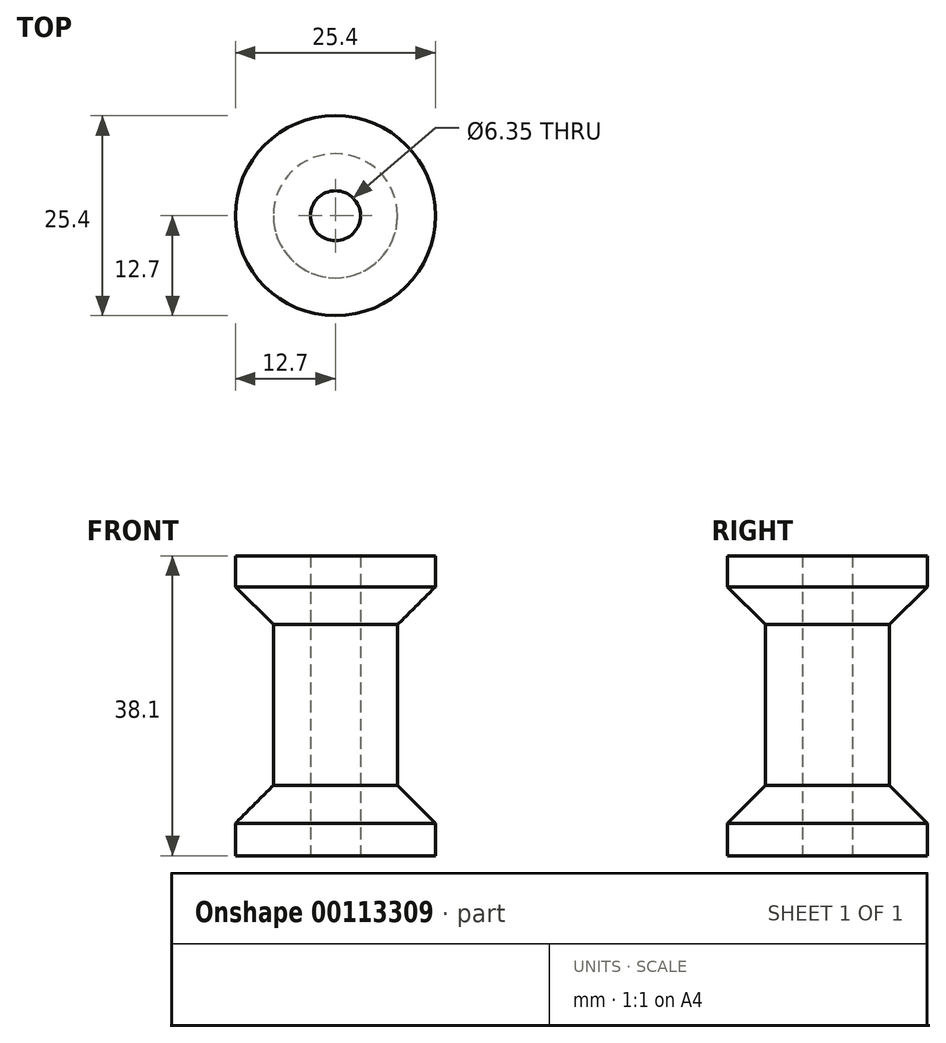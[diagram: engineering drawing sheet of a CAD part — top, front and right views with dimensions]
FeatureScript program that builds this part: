
annotation { "Feature Type Name" : "Feature", "Feature Type Description" : "" }
export const myFeature = defineFeature(function(context is Context, id is Id, definition is map)
    precondition{}
    {
        {
            var Q0;
            Q0=qCreatedBy(makeId("Top.planeOp"),FACE);
            var sketch = newSketch(context, id + "F0", { "sketchPlane" : qUnion([Q0])});
            skCircle(sketch, "E0", {"center": v(0, 0) * mm, "radius": 12.7 * mm});
            skSolve(sketch);
        }
        {
            var Q0;
            Q0=makeQuery(id+"F0.imprint","IMPRINT",FACE,{"disambiguationData":[TD([[makeQuery(id+"F0.imprint","IMPRINT",EDGE,{"derivedFrom":sQuery(id+"F0.wireOp",EDGE,"E0")}),1.0]])]});
            extrude(context, id + "F1", {"entities" : qUnion([Q0]), "depth" : 38.1 * mm});
        }
        {
            var Q0;
            Q0=qCreatedBy(makeId("Right.planeOp"),FACE);
            var sketch = newSketch(context, id + "F2", { "sketchPlane" : qUnion([Q0])});
            skLineSegment(sketch, "E1.bottom", {"start": v(-18.15, 34.43) * mm, "end": v(-7.9, 34.43) * mm});
            skLineSegment(sketch, "E1.top", {"start": v(-18.15, 3.85) * mm, "end": v(-7.9, 3.85) * mm});
            skLineSegment(sketch, "E1.left", {"start": v(-18.15, 34.43) * mm, "end": v(-18.15, 3.85) * mm});
            skLineSegment(sketch, "E1.right", {"start": v(-7.9, 34.43) * mm, "end": v(-7.9, 3.85) * mm});
            skLineSegment(sketch, "E2", {"start": v(0, 45.88) * mm, "end": v(0, -8) * mm});
            skSolve(sketch);
        }
        {
            var Q0;
            Q0=makeQuery(id+"F2.imprint","IMPRINT",FACE,{"disambiguationData":[TD([[makeQuery(id+"F2.imprint","IMPRINT",EDGE,{"derivedFrom":sQuery(id+"F2.wireOp",EDGE,"E1.bottom")}),-1.0]])]});
            var Q1;
            Q1=sQuery(id+"F2.wireOp",EDGE,"E2");
            revolve(context, id + "F3", {"operationType" : NewBodyOperationType.REMOVE, "entities" : qUnion([Q0]), "axis" : qUnion([Q1]), "revolveType" : RevolveType.FULL, "oppositeDirection" : true});
        }
        {
            var Q0;
            Q0=makeQuery(id+"F1.opExtrude","CAP_FACE",FACE,{"disambiguationData":[OSD([sQuery(id+"F0.wireOp",EDGE,"E0")])],"isStart":true});
            var sketch = newSketch(context, id + "F4", { "sketchPlane" : qUnion([Q0])});
            skCircle(sketch, "E3", {"center": v(0, 0) * mm, "radius": 3.18 * mm});
            skSolve(sketch);
        }
        {
            var Q0;
            Q0 = qSketchRegion(id + "F4", true);
            extrude(context, id + "F5", {"entities" : qUnion([Q0]), "operationType" : NewBodyOperationType.REMOVE, "oppositeDirection" : true, "depth" : 50.8 * mm});
        }
        {
            var Q0;
            Q0=makeQuery(id+"F3.boolean.opBoolean","COPY",EDGE,{"derivedFrom":makeQuery(id+"F3.opRevolve","SWEPT_EDGE",EDGE,{"disambiguationData":[OSD([sQuery(id+"F2.wireOp",EDGE,"E1.top"),sQuery(id+"F2.wireOp",EDGE,"E1.right")])]})});
            var Q1;
            Q1=makeQuery(id+"F3.boolean.opBoolean","COPY",EDGE,{"derivedFrom":makeQuery(id+"F3.opRevolve","SWEPT_EDGE",EDGE,{"disambiguationData":[OSD([sQuery(id+"F2.wireOp",EDGE,"E1.bottom"),sQuery(id+"F2.wireOp",EDGE,"E1.right")])]})});
            chamfer(context, id + "F6", {"entities" : qUnion([Q0, Q1]), "width" : 5.08 * mm, "tangentPropagation" : true});
        }
    });
